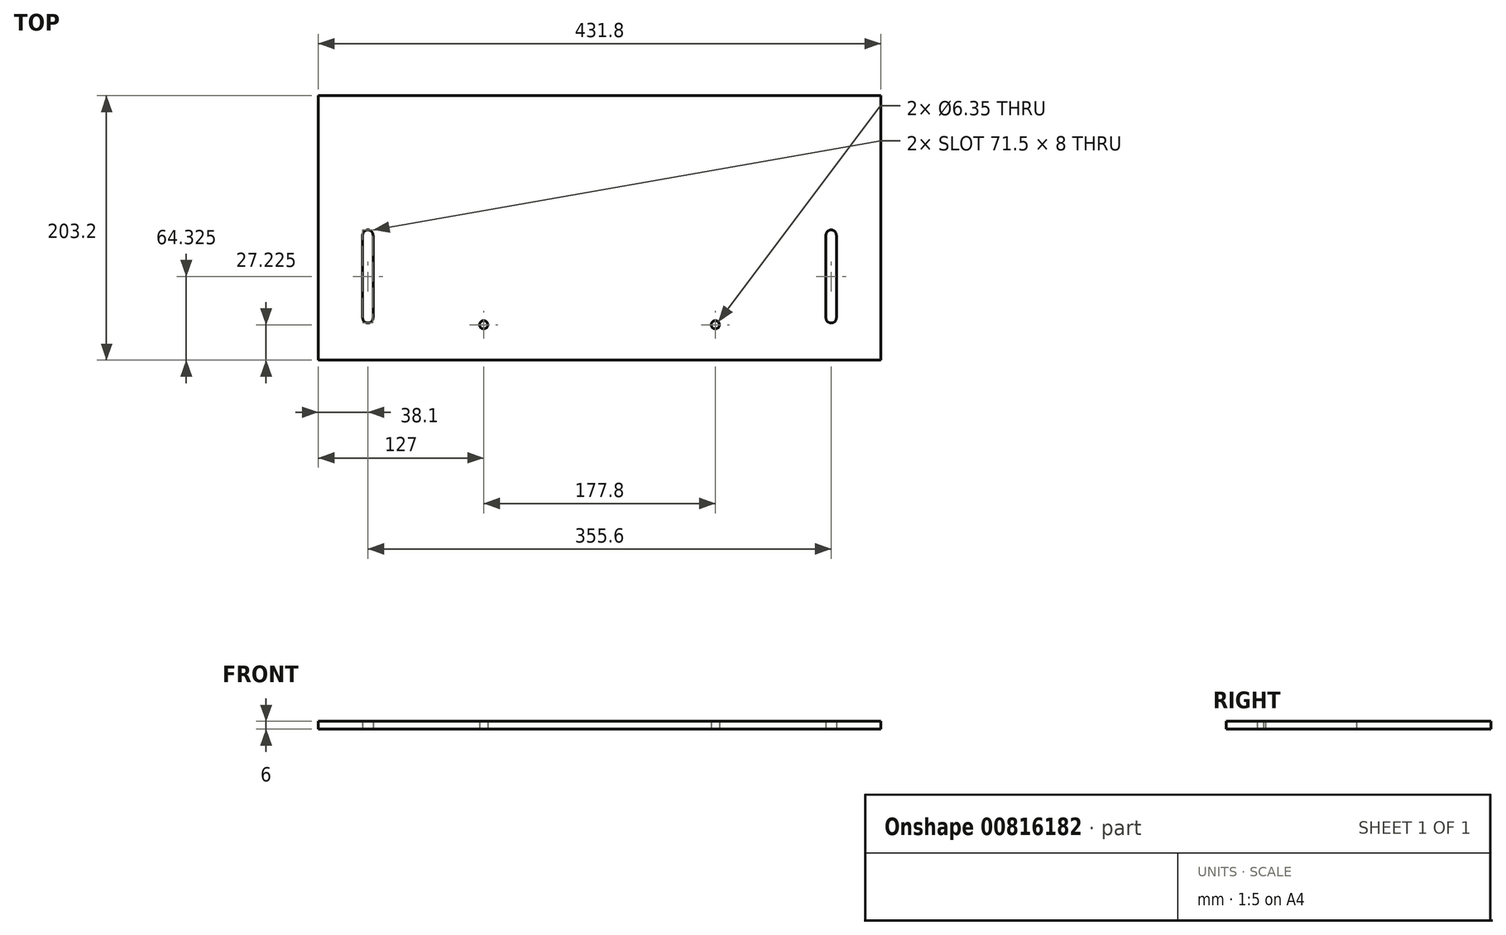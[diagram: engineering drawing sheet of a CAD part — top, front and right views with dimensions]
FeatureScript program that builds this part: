
annotation { "Feature Type Name" : "Feature", "Feature Type Description" : "" }
export const myFeature = defineFeature(function(context is Context, id is Id, definition is map)
    precondition{}
    {
        {
            var Q0;
            Q0=qCreatedBy(makeId("Top.planeOp"),FACE);
            var sketch = newSketch(context, id + "F0", { "sketchPlane" : qUnion([Q0])});
            skLineSegment(sketch, "E0.bottom", {"start": v(-215.9, 101.6) * mm, "end": v(215.9, 101.6) * mm});
            skLineSegment(sketch, "E0.top", {"start": v(-215.9, -101.6) * mm, "end": v(215.9, -101.6) * mm});
            skLineSegment(sketch, "E0.left", {"start": v(-215.9, 101.6) * mm, "end": v(-215.9, -101.6) * mm});
            skLineSegment(sketch, "E0.right", {"start": v(215.9, 101.6) * mm, "end": v(215.9, -101.6) * mm});
            skPoint(sketch, "E0.middle", {"position": v(0, 0) * mm});
            skLineSegment(sketch, "E1", {"start": v(0, 101.6) * mm, "end": v(0, -101.6) * mm, "construction": true});
            skLineSegment(sketch, "E2", {"start": v(-215.9, 0) * mm, "end": v(215.9, 0) * mm, "construction": true});
            skLineSegment(sketch, "E3", {"start": v(-177.8, -5.53) * mm, "end": v(-177.8, -69.03) * mm});
            skArc(sketch, "E4.0.startCap", {"start": v(-181.8, -5.53) * mm, "mid": v(-177.8, -1.53) * mm, "end": v(-173.8, -5.53) * mm});
            skArc(sketch, "E4.0.endCap", {"start": v(-173.8, -69.03) * mm, "mid": v(-177.8, -73.03) * mm, "end": v(-181.8, -69.03) * mm});
            skLineSegment(sketch, "E4.0.left", {"start": v(-173.8, -5.53) * mm, "end": v(-173.8, -69.03) * mm});
            skLineSegment(sketch, "E4.0.right", {"start": v(-181.8, -5.53) * mm, "end": v(-181.8, -69.03) * mm});
            skArc(sketch, "E5.MirrorCS", {"start": v(173.8, -69.03) * mm, "mid": v(177.8, -73.03) * mm, "end": v(181.8, -69.03) * mm});
            skLineSegment(sketch, "E6.MirrorCS", {"start": v(181.8, -5.53) * mm, "end": v(181.8, -69.03) * mm});
            skArc(sketch, "E7.MirrorCS", {"start": v(181.8, -5.53) * mm, "mid": v(177.8, -1.53) * mm, "end": v(173.8, -5.53) * mm});
            skLineSegment(sketch, "E8.MirrorCS", {"start": v(173.8, -5.53) * mm, "end": v(173.8, -69.03) * mm});
            skLineSegment(sketch, "E9.MirrorCS", {"start": v(177.8, -5.53) * mm, "end": v(177.8, -69.03) * mm});
            skLineSegment(sketch, "E10.top", {"start": v(-50.8, -101.32) * mm, "end": v(-127, -101.32) * mm});
            skPoint(sketch, "E10.middle", {"position": v(-88.9, -56.87) * mm});
            skPoint(sketch, "E11.visualSharp", {"position": v(-127, -12.42) * mm});
            skPoint(sketch, "E12.visualSharp", {"position": v(-50.8, -12.42) * mm});
            skLineSegment(sketch, "E13", {"start": v(-50.8, -56.87) * mm, "end": v(-127, -56.87) * mm, "construction": true});
            skLineSegment(sketch, "E14", {"start": v(-88.9, -12.42) * mm, "end": v(-88.9, -101.32) * mm, "construction": true});
            skLineSegment(sketch, "E15.MirrorCS", {"start": v(-88.9, -101.32) * mm, "end": v(-88.9, -12.42) * mm, "construction": true});
            skLineSegment(sketch, "E16", {"start": v(-177.8, -69.03) * mm, "end": v(-177.8, -101.6) * mm, "construction": true});
            skPoint(sketch, "E16.endSnap0", {"position": v(-177.8, -73.03) * mm});
            skLineSegment(sketch, "E17.MirrorCS", {"start": v(88.9, -101.32) * mm, "end": v(88.9, -12.42) * mm, "construction": true});
            skLineSegment(sketch, "E18.MirrorCS", {"start": v(50.8, -56.87) * mm, "end": v(127, -56.87) * mm, "construction": true});
            skPoint(sketch, "E19.MirrorP", {"position": v(127, -12.42) * mm});
            skLineSegment(sketch, "E20.MirrorCS", {"start": v(88.9, -12.42) * mm, "end": v(88.9, -101.32) * mm, "construction": true});
            skPoint(sketch, "E21.MirrorP", {"position": v(88.9, -56.87) * mm});
            skLineSegment(sketch, "E22.MirrorCS", {"start": v(50.8, -101.32) * mm, "end": v(127, -101.32) * mm});
            skCircle(sketch, "E23", {"center": v(-88.9, -74.37) * mm, "radius": 3.17 * mm});
            skCircle(sketch, "E24.MirrorC", {"center": v(88.9, -74.37) * mm, "radius": 3.17 * mm});
            skSolve(sketch);
        }
        {
            var Q0;
            Q0=makeQuery(id+"F0.imprint","IMPRINT",FACE,{"disambiguationData":[TD([[makeQuery(id+"F0.imprint","IMPRINT",EDGE,{"derivedFrom":sQuery(id+"F0.wireOp",EDGE,"E0.bottom")}),-1.0]])]});
            extrude(context, id + "F1", {"entities" : qUnion([Q0]), "endBound" : BoundingType.SYMMETRIC, "depth" : 6 * mm, "offsetDistance" : 25 * mm});
        }
    });
